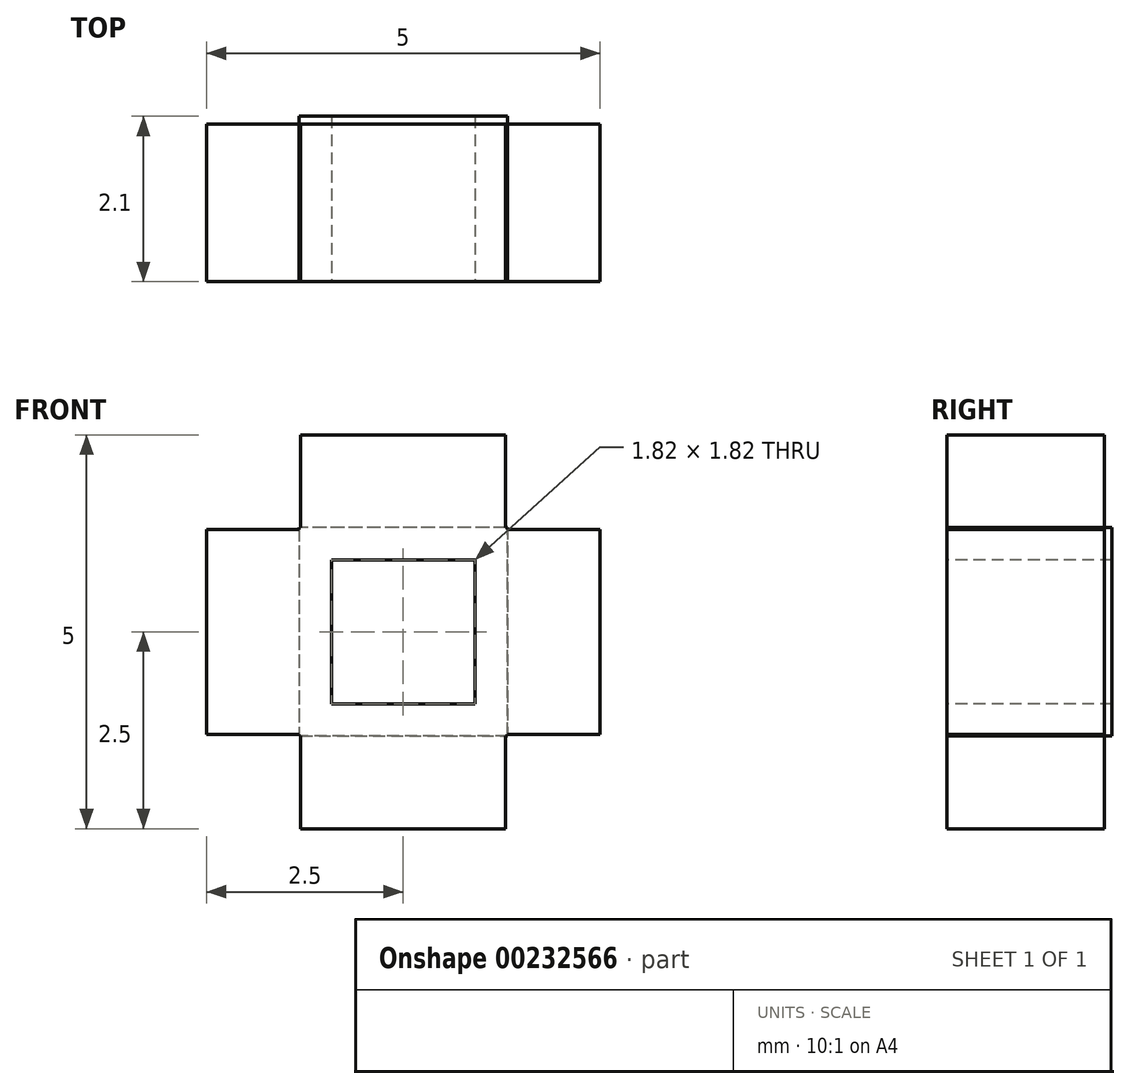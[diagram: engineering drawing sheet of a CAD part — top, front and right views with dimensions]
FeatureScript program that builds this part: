
annotation { "Feature Type Name" : "Feature", "Feature Type Description" : "" }
export const myFeature = defineFeature(function(context is Context, id is Id, definition is map)
    precondition{}
    {
        {
            var Q0;
            Q0=qCreatedBy(makeId("Front.planeOp"),FACE);
            var sketch = newSketch(context, id + "F0", { "sketchPlane" : qUnion([Q0])});
            skLineSegment(sketch, "E0.bottom", {"start": v(1.33, 1.32) * mm, "end": v(-1.32, 1.32) * mm});
            skLineSegment(sketch, "E0.top", {"start": v(1.32, -1.33) * mm, "end": v(-1.33, -1.33) * mm});
            skLineSegment(sketch, "E0.left", {"start": v(1.32, 1.32) * mm, "end": v(1.32, -1.33) * mm});
            skLineSegment(sketch, "E0.right", {"start": v(-1.32, 1.32) * mm, "end": v(-1.33, -1.33) * mm});
            skPoint(sketch, "E0.middle", {"position": v(0, 0) * mm});
            skSolve(sketch);
        }
        {
            var Q0;
            Q0 = qSketchRegion(id + "F0", true);
            extrude(context, id + "F1", {"entities" : qUnion([Q0]), "depth" : 2.1 * mm});
        }
        {
            var Q0;
            Q0=makeQuery(id+"F1.opExtrude","SWEPT_FACE",FACE,{"disambiguationData":[OSD([sQuery(id+"F0.wireOp",EDGE,"E0.top")])]});
            var sketch = newSketch(context, id + "F2", { "sketchPlane" : qUnion([Q0])});
            skLineSegment(sketch, "E1", {"start": v(-1.33, 2.1) * mm, "end": v(-1.33, 2.1) * mm});
            skLineSegment(sketch, "E2", {"start": v(-1.33, 2.1) * mm, "end": v(-1.3, 2.1) * mm});
            skLineSegment(sketch, "E3.bottom", {"start": v(-1.3, 2.1) * mm, "end": v(1.3, 2.1) * mm});
            skLineSegment(sketch, "E3.top", {"start": v(-1.3, 0.1) * mm, "end": v(1.3, 0.1) * mm});
            skLineSegment(sketch, "E3.left", {"start": v(-1.3, 2.1) * mm, "end": v(-1.3, 0.1) * mm});
            skLineSegment(sketch, "E3.right", {"start": v(1.3, 2.1) * mm, "end": v(1.3, 0.1) * mm});
            skSolve(sketch);
        }
        {
            var Q0;
            Q0 = qSketchRegion(id + "F2", true);
            extrude(context, id + "F3", {"entities" : qUnion([Q0]), "operationType" : NewBodyOperationType.ADD, "depth" : 1.18 * mm});
        }
        {
            var Q0;
            Q0=makeQuery(id+"F1.opExtrude","SWEPT_FACE",FACE,{"disambiguationData":[OSD([sQuery(id+"F0.wireOp",EDGE,"E0.right")])]});
            var sketch = newSketch(context, id + "F4", { "sketchPlane" : qUnion([Q0])});
            skLineSegment(sketch, "E4", {"start": v(2.1, 1.32) * mm, "end": v(2.1, 1.32) * mm});
            skLineSegment(sketch, "E5", {"start": v(2.1, 1.32) * mm, "end": v(2.1, 1.3) * mm});
            skLineSegment(sketch, "E6.bottom", {"start": v(2.1, 1.3) * mm, "end": v(0.1, 1.3) * mm});
            skLineSegment(sketch, "E6.top", {"start": v(2.1, -1.3) * mm, "end": v(0.1, -1.3) * mm});
            skLineSegment(sketch, "E6.left", {"start": v(2.1, 1.3) * mm, "end": v(2.1, -1.3) * mm});
            skLineSegment(sketch, "E6.right", {"start": v(0.1, 1.3) * mm, "end": v(0.1, -1.3) * mm});
            skSolve(sketch);
        }
        {
            var Q0;
            Q0 = qSketchRegion(id + "F4", true);
            extrude(context, id + "F5", {"entities" : qUnion([Q0]), "operationType" : NewBodyOperationType.ADD, "depth" : 1.18 * mm});
        }
        {
            var Q0;
            Q0=makeQuery(id+"F1.opExtrude","SWEPT_FACE",FACE,{"disambiguationData":[OSD([sQuery(id+"F0.wireOp",EDGE,"E0.bottom")])]});
            var sketch = newSketch(context, id + "F6", { "sketchPlane" : qUnion([Q0])});
            skLineSegment(sketch, "E7", {"start": v(1.33, -2.1) * mm, "end": v(1.33, -2.1) * mm});
            skLineSegment(sketch, "E8", {"start": v(1.33, -2.1) * mm, "end": v(1.3, -2.1) * mm});
            skLineSegment(sketch, "E9.bottom", {"start": v(1.3, -2.1) * mm, "end": v(-1.3, -2.1) * mm});
            skLineSegment(sketch, "E9.top", {"start": v(1.3, -0.1) * mm, "end": v(-1.3, -0.1) * mm});
            skLineSegment(sketch, "E9.left", {"start": v(1.3, -2.1) * mm, "end": v(1.3, -0.1) * mm});
            skLineSegment(sketch, "E9.right", {"start": v(-1.3, -2.1) * mm, "end": v(-1.3, -0.1) * mm});
            skSolve(sketch);
        }
        {
            var Q0;
            Q0 = qSketchRegion(id + "F6", true);
            extrude(context, id + "F7", {"entities" : qUnion([Q0]), "operationType" : NewBodyOperationType.ADD, "depth" : 1.18 * mm});
        }
        {
            var Q0;
            Q0=makeQuery(id+"F1.opExtrude","SWEPT_FACE",FACE,{"disambiguationData":[OSD([sQuery(id+"F0.wireOp",EDGE,"E0.left")])]});
            var sketch = newSketch(context, id + "F8", { "sketchPlane" : qUnion([Q0])});
            skLineSegment(sketch, "E10", {"start": v(-2.1, -1.33) * mm, "end": v(-2.1, -1.33) * mm});
            skLineSegment(sketch, "E11", {"start": v(-2.1, -1.33) * mm, "end": v(-2.1, -1.3) * mm});
            skLineSegment(sketch, "E12.bottom", {"start": v(-2.1, -1.3) * mm, "end": v(-0.1, -1.3) * mm});
            skLineSegment(sketch, "E12.top", {"start": v(-2.1, 1.3) * mm, "end": v(-0.1, 1.3) * mm});
            skLineSegment(sketch, "E12.left", {"start": v(-2.1, -1.3) * mm, "end": v(-2.1, 1.3) * mm});
            skLineSegment(sketch, "E12.right", {"start": v(-0.1, -1.3) * mm, "end": v(-0.1, 1.3) * mm});
            skSolve(sketch);
        }
        {
            var Q0;
            Q0 = qSketchRegion(id + "F8", true);
            extrude(context, id + "F9", {"entities" : qUnion([Q0]), "operationType" : NewBodyOperationType.ADD, "depth" : 1.18 * mm});
        }
        {
            var Q0;
            Q0=makeQuery(id+"F1.opExtrude","CAP_FACE",FACE,{"disambiguationData":[OSD([sQuery(id+"F0.wireOp",EDGE,"E0.bottom"),sQuery(id+"F0.wireOp",EDGE,"E0.top"),sQuery(id+"F0.wireOp",EDGE,"E0.left"),sQuery(id+"F0.wireOp",EDGE,"E0.right")])],"isStart":false});
            var sketch = newSketch(context, id + "F10", { "sketchPlane" : qUnion([Q0])});
            skLineSegment(sketch, "E13", {"start": v(1.31, -1.33) * mm, "end": v(1.31, 1.32) * mm});
            skLineSegment(sketch, "E14", {"start": v(1.32, 1.31) * mm, "end": v(-1.32, 1.31) * mm});
            skPoint(sketch, "E15", {"position": v(0, 0) * mm});
            skLineSegment(sketch, "E16.bottom", {"start": v(-0.91, -0.91) * mm, "end": v(0.91, -0.91) * mm});
            skLineSegment(sketch, "E16.top", {"start": v(-0.91, 0.91) * mm, "end": v(0.91, 0.91) * mm});
            skLineSegment(sketch, "E16.left", {"start": v(-0.91, -0.91) * mm, "end": v(-0.91, 0.91) * mm});
            skLineSegment(sketch, "E16.right", {"start": v(0.91, -0.91) * mm, "end": v(0.91, 0.91) * mm});
            skSolve(sketch);
        }
        {
            var Q0;
            Q0 = qSketchRegion(id + "F10", true);
            extrude(context, id + "F11", {"entities" : qUnion([Q0]), "operationType" : NewBodyOperationType.REMOVE, "oppositeDirection" : true, "depth" : 2.1 * mm});
        }
    });
